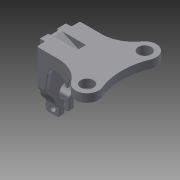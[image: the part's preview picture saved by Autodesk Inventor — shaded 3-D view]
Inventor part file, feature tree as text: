
AUTODESK INVENTOR PART (.ipt)
format: ipt  version: 2014 (Build 180170000, 170)  size: 567,296 bytes
history: native  units: in
note: dims shown in document units (in); Inventor stores cm internally (conversion verified against a paired STEP export)
features: extrude x10, sketch x10, fillet x7, mirror x1
ambient origin geometry x8: Origin, YZ Plane, XZ Plane, XY Plane, X Axis, Y Axis, Z Axis, Center Point
bodies: Solid1 (feature_tree)
feature tree (28):
  extrude  "Extrusion1"  Depth=1.0441in
  extrude  "Extrusion2"  Depth=0.3543in
  extrude  "Extrusion3"  Depth=1.1811in
  mirror  "Mirror1"
  extrude  "Extrusion4"  Depth=0.9843in
  extrude  "Extrusion5"  Depth=0.2362in TaperAngle=0.0deg
  extrude  "Extrusion6"  Depth=1.5748in
  extrude  "Extrusion7"  Depth=0.3346in
  extrude  "Extrusion8"  Depth=0.5906in TaperAngle=0.0deg
  extrude  "Extrusion9"  Depth=0.1181in TaperAngle=0.0deg
  extrude  "Extrusion10"  Depth=0.0394in
  fillet  "Fillet1"  Radius=1.5748in
  fillet  "Fillet2"  Radius=0.3937in
  fillet  "Fillet3"  Radius=0.0394in
  fillet  "Fillet4"  Radius=0.1575in
  fillet  "Fillet5"  Radius=0.2756in
  fillet  "Fillet6"  Radius=0.5906in
  fillet  "Fillet7"  Radius=0.3937in
  sketch  "Sketch1"  dims[d0=1.1713in d1=1.0441in]
  sketch  "Sketch2"  dims[d2=1.5748in d3=0.3543in]
  sketch  "Sketch3"  dims[d4=0.6299in d5=1.1811in]
  sketch  "Sketch4"  dims[d6=0.5906in d7=0.9843in]
  sketch  "Sketch5"  dims[d8=1.7717in d9=0.2362in d10=0.0in]
  sketch  "Sketch6"  dims[d11=0.2362in d12=1.5748in]
  sketch  "Sketch7"  dims[d13=0.5945in d15=0.3346in]
  sketch  "Sketch8"  dims[d16=0.1181in d17=0.5906in d18=0.5906in d19=0.0in d20=0.0in]
  sketch  "Sketch9"  dims[d21=0.0591in d22=0.1181in d23=0.0in]
  sketch  "Sketch10"  dims[d24=0.3937in d25=0.0394in d26=1.5748in d27=0.0in d28=0.3937in d29=0.0394in d30=0.1575in d31=0.2756in d32=0.5906in d33=0.3937in d34=0.0in d35=0.7087in d36=0.1575in d37=0.0in d38=0.1181in d39=0.2756in d40=0.1181in d41=0.4724in d42=0.0in d43=0.1378in d44=0.3937in d45=0.4724in d46=0.0in d47=0.1319in d48=0.4724in d49=0.0in d50=0.1969in d51=0.1969in d52=0.1181in d53=0.1181in d54=0.1181in d55=0.0in d56=0.0in d57=0.0787in d58=0.0394in d59=0.0197in d60=0.0197in d61=0.0197in d62=0.0197in d63=0.0197in]
